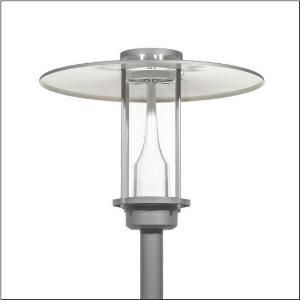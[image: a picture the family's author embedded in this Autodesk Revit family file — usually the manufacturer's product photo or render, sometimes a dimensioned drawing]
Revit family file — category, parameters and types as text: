
# Revit family: city-light_plus_iq___p1_0a_5xa5275ff14h000022_8535
name_source: partatom
category: Lighting Fixtures
units: mm (PartAtom-declared; Revit-internal decimal feet)

## family parameters
Cut with Voids When Loaded = No
Host = Face
Light Source = No
Part Type = Normal
Room Calculation Point = No
Round Connector Dimension = Use Diameter
Shared = No

## types (1)
- --- (1 x LED, 1440 lm, 10.5 W, 3000K)
    Apparent Load = 11 VA
    CIE Flux Codes = 32 61 90 96 100
    Color Rendering = 70
    Color Temperature = 3000K
    Default Elevation = 1800 mm
    Description = City-Light Plus iQ, mast luminaire, Module 540 iQ-SR, primary light control with 3 zone facetted reflector, of plastic, silver coated, highly specular, structured, primary optical cover: cover, of PMMA, transparent, light distribution: P1.0a, light emission: direct distribution, primary light characteristic: strongly asymmetric, installation type: post-top, LED, High Power LED, rated luminous flux: 1.440lm, luminous efficacy: 137lm/W, light colour: 730, colour temperature: 3000K, control gear: ECG iQ, control: Street-Remote, Auto-Match, Temp-Guard, Lumen-Switch, Night-Set, Smart-Wire, Light-Fading, Desk-Remote (wireless, voltage-free reading and setting of iQ features in the workshop via application-optimized NFC function/RFID function), optimised constant luminous flux control (CLO 2.0), pre-setting: logarithmic dimming characteristic, mains connection: 230..240V, AC, 50/60Hz, connection cable pre-assembled, cable length: 5,5m, wiring characteristics: H07RN-F, start of lifetime: 11W, end of service life: 11W, reduction: 5W, luminaire housing, upper part, of glass-fibre reinforced polyester, coated, Siteco® metallic grey (DB 702S), diameter: 750mm, height: 590mm, spigot size: d x l = 76 x 70mm (post-top) | with reducer (optional accessory) 60 x 70mm, post-top mast mounting element, of diecast aluminium, coated, Siteco® metallic grey (DB 702S), Module 540 iQ-SR, traffic white (RAL 9016), equipment: standard, protection rating (complete): IP65, insulation class (complete): insulation class II (safety insulation), certification: CE, ENEC, VDE, packaging unit: 1 piece

Light Distribution: P1.0a
    Height = 590 mm
    Lamp = 1 x LED
    Lamp Light Flux = 1440 lm
    Lamp Power = 10.5 W
    Lamp count = 1
    Length = 750 mm
    Luminous efficacy = 137 lm/W
    Manufacturer = Siteco
    ModVariant = No
    Model = 5XA5275FF14H000022
    Number of Poles = 1
    OnlyDefault = Yes
    Power Factor = 1
    Product Name = City-Light Plus iQ | P1.0a
    Product group = mast luminaire | pylon top
    ProductGroupID = 6100
    Protection Class = Protection class II
    Protection Degree = IP 65
    RLX_Detail_Level = 1
    RLX_Emergency_Light_Flux = 0 lm
    RLX_Emergency_Type = 0
    RLX_Emergency_Type_DB = No
    RlxData = <blob elided: 51757 chars, md5=57bf6e2c>
    Socket = socket
    Standby Power = 0 W
    System Light Flux = 1440 lm
    System Power = 11 W
    Type Comments = factory setting: luminous flux: 100 % | dim-lin: 254 | 419 mA
    Type Image = l_1006456.jpg
    URL = http://relux.com
    VarID = @adj_130279
    Voltage = 0 V
    Weight = 0.00 kg
    Width = 0 mm  [stored 0 ft]

note: [stored X ft] marks values corroborated as IEEE doubles in the binary element streams (Revit-internal decimal feet)

## geometry (parser evidence)
native form markers: Blend x4, Sweep x10
no freeform markers — native parametric forms only
